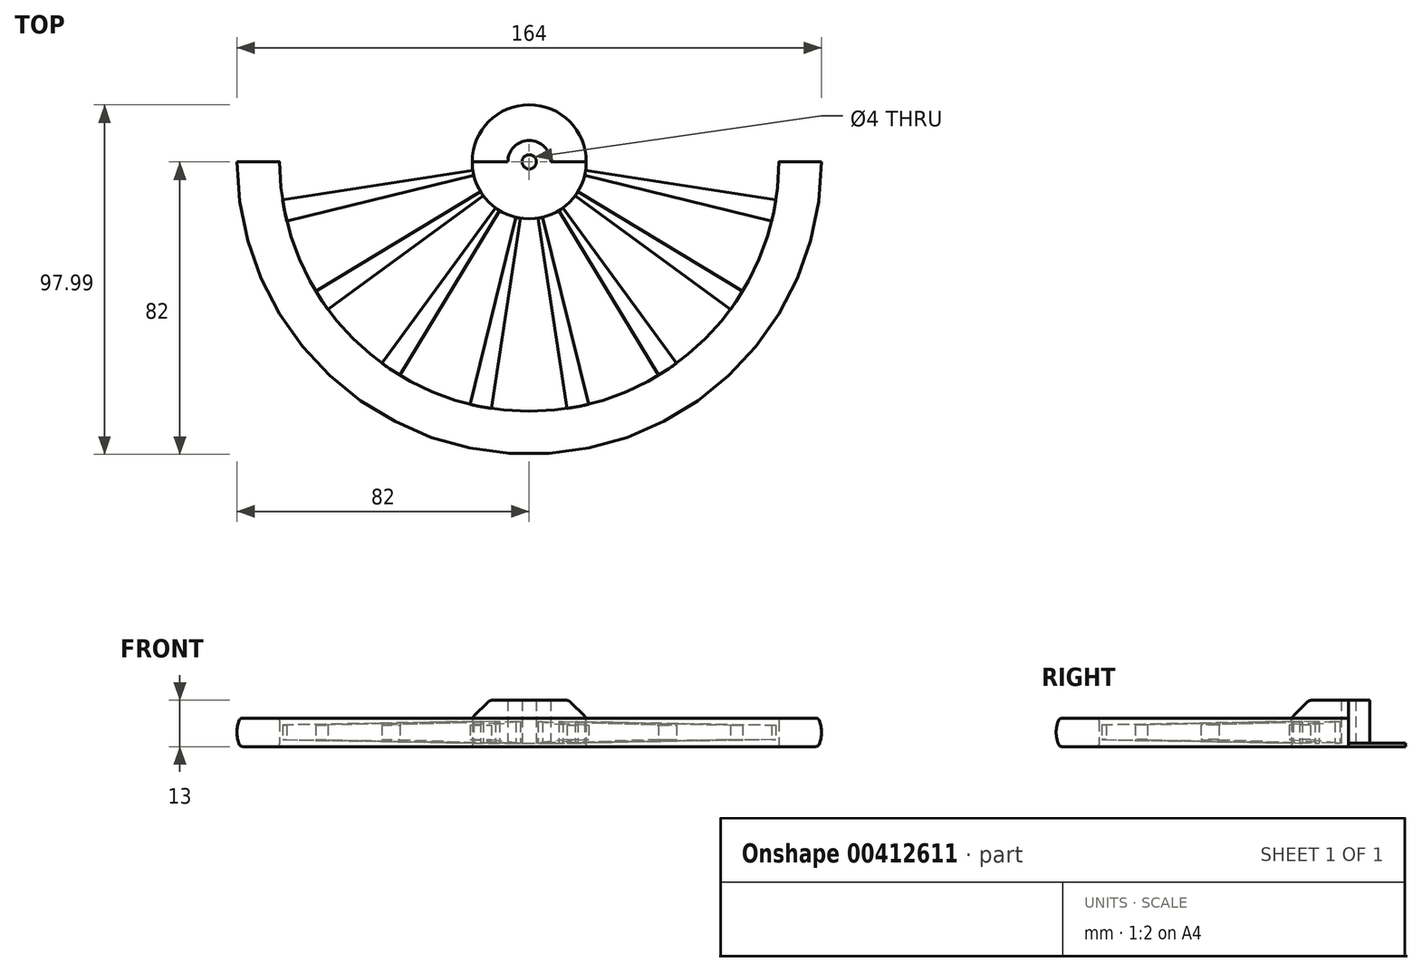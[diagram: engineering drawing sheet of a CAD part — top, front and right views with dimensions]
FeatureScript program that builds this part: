
annotation { "Feature Type Name" : "Feature", "Feature Type Description" : "" }
export const myFeature = defineFeature(function(context is Context, id is Id, definition is map)
    precondition{}
    {
        {
            var Q0;
            Q0=qCreatedBy(makeId("Front.planeOp"),FACE);
            var sketch = newSketch(context, id + "F0", { "sketchPlane" : qUnion([Q0])});
            skLineSegment(sketch, "E0", {"start": v(-2, 0) * mm, "end": v(-2, 13) * mm});
            skLineSegment(sketch, "E1", {"start": v(-2, 13) * mm, "end": v(-10.24, 13) * mm});
            skLineSegment(sketch, "E2", {"start": v(-16, 7.24) * mm, "end": v(-16, 0) * mm});
            skLineSegment(sketch, "E3", {"start": v(-16, 0) * mm, "end": v(-2, 0) * mm});
            skLineSegment(sketch, "E4", {"start": v(-15.4, 8.66) * mm, "end": v(-11.65, 12.41) * mm});
            skPoint(sketch, "E5.visualSharp", {"position": v(-11.07, 13) * mm});
            skArc(sketch, "E5.filletArc", {"start": v(-10.24, 13) * mm, "mid": v(-11, 12.85) * mm, "end": v(-11.65, 12.41) * mm});
            skPoint(sketch, "E6.visualSharp", {"position": v(-16, 8.07) * mm});
            skArc(sketch, "E6.filletArc", {"start": v(-15.4, 8.66) * mm, "mid": v(-15.84, 8) * mm, "end": v(-16, 7.24) * mm});
            skSolve(sketch);
        }
        {
            var Q0;
            Q0=qCreatedBy(makeId("Front.planeOp"),FACE);
            var sketch = newSketch(context, id + "F1", { "sketchPlane" : qUnion([Q0])});
            skLineSegment(sketch, "E7", {"start": v(0, 0) * mm, "end": v(0, 15.4) * mm, "construction": true});
            skSolve(sketch);
        }
        {
            var Q0;
            Q0 = qSketchRegion(id + "F0", true);
            var Q1;
            Q1=sQuery(id+"F1.wireOp",EDGE,"E7");
            revolve(context, id + "F2", {"entities" : qUnion([Q0]), "axis" : qUnion([Q1]), "revolveType" : RevolveType.ONE_DIRECTION, "angle" : 180 * degree});
        }
        {
            var Q0;
            Q0=qCreatedBy(makeId("Front.planeOp"),FACE);
            var sketch = newSketch(context, id + "F3", { "sketchPlane" : qUnion([Q0])});
            skLineSegment(sketch, "E8", {"start": v(-70.8, 0) * mm, "end": v(-80.37, 0) * mm});
            skLineSegment(sketch, "E9", {"start": v(-82, 0) * mm, "end": v(-82, 8) * mm, "construction": true});
            skLineSegment(sketch, "E10", {"start": v(-80.37, 8) * mm, "end": v(-70.75, 8) * mm});
            skLineSegment(sketch, "E11", {"start": v(-70, 7.25) * mm, "end": v(-70, 0.8) * mm});
            skLineSegment(sketch, "E12", {"start": v(-81, 8) * mm, "end": v(-81, 0) * mm, "construction": true});
            skArc(sketch, "E13", {"start": v(-81.3, 7.4) * mm, "mid": v(-82, 4) * mm, "end": v(-81.3, 0.6) * mm});
            skPoint(sketch, "E14.visualSharp", {"position": v(-81, 8) * mm});
            skArc(sketch, "E14.filletArc", {"start": v(-80.37, 8) * mm, "mid": v(-80.92, 7.84) * mm, "end": v(-81.3, 7.4) * mm});
            skPoint(sketch, "E15.visualSharp", {"position": v(-81, 0) * mm});
            skArc(sketch, "E15.filletArc", {"start": v(-81.3, 0.6) * mm, "mid": v(-80.92, 0.16) * mm, "end": v(-80.37, 0) * mm});
            skPoint(sketch, "E16.visualSharp", {"position": v(-70, 8) * mm});
            skArc(sketch, "E16.filletArc", {"start": v(-70, 7.25) * mm, "mid": v(-70.22, 7.78) * mm, "end": v(-70.75, 8) * mm});
            skPoint(sketch, "E17.visualSharp", {"position": v(-70, 0) * mm});
            skArc(sketch, "E17.filletArc", {"start": v(-70.8, 0) * mm, "mid": v(-70.23, 0.23) * mm, "end": v(-70, 0.8) * mm});
            skSolve(sketch);
        }
        {
            var Q0;
            Q0 = qSketchRegion(id + "F3", true);
            var Q1;
            Q1=sQuery(id+"F1.wireOp",EDGE,"E7");
            revolve(context, id + "F4", {"entities" : qUnion([Q0]), "axis" : qUnion([Q1]), "revolveType" : RevolveType.ONE_DIRECTION, "angle" : 180 * degree});
        }
        {
            var Q0;
            Q0=sQuery(id+"F1.wireOp",EDGE,"E7");
            var Q1;
            Q1=qCreatedBy(makeId("Front.planeOp"),FACE);
            cPlane(context, id + "F5", {"entities" : qUnion([Q0, Q1]), "cplaneType" : CPlaneType.LINE_ANGLE, "offset" : 25 * mm, "angle" : 11.25 * degree, "width" : 150 * mm, "height" : 150 * mm});
        }
        {
            var Q0;
            Q0=qCreatedBy(makeId("Top.planeOp"),FACE);
            cPlane(context, id + "F6", {"entities" : qUnion([Q0]), "cplaneType" : CPlaneType.OFFSET, "offset" : 1 * mm, "width" : 150 * mm, "height" : 150 * mm});
        }
        {
            var Q0;
            Q0=qCreatedBy(id+"F6.planeOp",FACE);
            var sketch = newSketch(context, id + "F7", { "sketchPlane" : qUnion([Q0])});
            skLineSegment(sketch, "E18", {"start": v(0, 0) * mm, "end": v(-68.65, -13.66) * mm, "construction": true});
            skLineSegment(sketch, "E19", {"start": v(0, 0) * mm, "end": v(-15.8, -2.43) * mm, "construction": true});
            skLineSegment(sketch, "E20", {"start": v(0, 0) * mm, "end": v(-15.54, -3.8) * mm, "construction": true});
            skLineSegment(sketch, "E21", {"start": v(-15.54, -3.8) * mm, "end": v(-15.54, -3.8) * mm});
            skPoint(sketch, "E22.orphan", {"position": v(-16, 0) * mm});
            skPoint(sketch, "E23.0.start.orphan", {"position": v(16, 0) * mm});
            skLineSegment(sketch, "E24", {"start": v(-15.8, -2.43) * mm, "end": v(-69.19, -10.65) * mm});
            skArc(sketch, "E25", {"start": v(-15.54, -3.8) * mm, "mid": v(-15.69, -3.12) * mm, "end": v(-15.8, -2.43) * mm});
            skLineSegment(sketch, "E26", {"start": v(-15.54, -3.8) * mm, "end": v(-68, -16.64) * mm});
            skArc(sketch, "E27.0", {"start": v(-68, -16.64) * mm, "mid": v(-68.65, -13.66) * mm, "end": v(-69.19, -10.65) * mm});
            skPoint(sketch, "E28.orphan", {"position": v(-70, 0) * mm});
            skPoint(sketch, "E29.orphan", {"position": v(70, 0) * mm});
            skSolve(sketch);
        }
        {
            var Q0;
            Q0 = qSketchRegion(id + "F7", true);
            extrude(context, id + "F8", {"entities" : qUnion([Q0]), "depth" : 6 * mm});
        }
        {
            var Q0;
            Q0=makeQuery(id+"F8.opExtrude","SWEPT_BODY",BODY,{"disambiguationData":[OSD([sQuery(id+"F7.wireOp",EDGE,"E24"),sQuery(id+"F7.wireOp",EDGE,"E25"),sQuery(id+"F7.wireOp",EDGE,"E26"),sQuery(id+"F7.wireOp",EDGE,"E27.0")])]});
            var Q1;
            Q1=sQuery(id+"F1.wireOp",EDGE,"E7");
            circularPattern(context, id + "F9", {"entities" : qUnion([Q0]), "axis" : qUnion([Q1]), "angle" : 157.5 * degree, "instanceCount" : 8, "equalSpace" : true});
        }
        {
            var Q0;
            Q0=qCreatedBy(makeId("Front.planeOp"),FACE);
            var sketch = newSketch(context, id + "F10", { "sketchPlane" : qUnion([Q0])});
            skLineSegment(sketch, "E30.0", {"start": v(-16, 7) * mm, "end": v(-70, 7) * mm});
            skPoint(sketch, "E31.orphan", {"position": v(-16, 7.24) * mm});
            skPoint(sketch, "E32.orphan", {"position": v(-15.8, 7) * mm});
            skLineSegment(sketch, "E33.0", {"start": v(-70, 7) * mm, "end": v(-70, 6.06) * mm});
            skPoint(sketch, "E34.orphan", {"position": v(-69.19, 7) * mm});
            skPoint(sketch, "E35.orphan", {"position": v(-70, 7.25) * mm});
            skLineSegment(sketch, "E36", {"start": v(-16, 7) * mm, "end": v(-70, 6.06) * mm});
            skPoint(sketch, "E37.orphan", {"position": v(-70, 0.8) * mm});
            skPoint(sketch, "E38.0.end.orphan", {"position": v(-16, 0) * mm});
            skSolve(sketch);
        }
        {
            var Q0;
            Q0 = qSketchRegion(id + "F10", true);
            var Q1;
            Q1=sQuery(id+"F1.wireOp",EDGE,"E7");
            revolve(context, id + "F11", {"operationType" : NewBodyOperationType.REMOVE, "entities" : qUnion([Q0]), "axis" : qUnion([Q1]), "revolveType" : RevolveType.FULL, "oppositeDirection" : true});
        }
        {
            var Q0;
            Q0=qCreatedBy(makeId("Front.planeOp"),FACE);
            var sketch = newSketch(context, id + "F12", { "sketchPlane" : qUnion([Q0])});
            skLineSegment(sketch, "E39.0", {"start": v(-70, 1.94) * mm, "end": v(-70, 1) * mm});
            skLineSegment(sketch, "E40.0", {"start": v(-16, 1) * mm, "end": v(-70, 1) * mm});
            skPoint(sketch, "E41.orphan", {"position": v(-69.19, 1) * mm});
            skPoint(sketch, "E42.orphan", {"position": v(-70, 0.8) * mm});
            skPoint(sketch, "E43.orphan", {"position": v(-15.8, 1) * mm});
            skPoint(sketch, "E44.orphan", {"position": v(-16, 0) * mm});
            skLineSegment(sketch, "E45", {"start": v(-16, 1) * mm, "end": v(-70, 1.94) * mm});
            skPoint(sketch, "E46.orphan", {"position": v(-70, 7.25) * mm});
            skPoint(sketch, "E47.0.start.orphan", {"position": v(-16, 7.24) * mm});
            skSolve(sketch);
        }
        {
            var Q0;
            Q0 = qSketchRegion(id + "F12", true);
            var Q1;
            Q1=sQuery(id+"F1.wireOp",EDGE,"E7");
            revolve(context, id + "F13", {"operationType" : NewBodyOperationType.REMOVE, "entities" : qUnion([Q0]), "axis" : qUnion([Q1]), "revolveType" : RevolveType.FULL, "oppositeDirection" : true});
        }
        {
            var Q0;
            Q0=qCreatedBy(makeId("Front.planeOp"),FACE);
            var sketch = newSketch(context, id + "F14", { "sketchPlane" : qUnion([Q0])});
            skLineSegment(sketch, "E48.0", {"start": v(2, 0) * mm, "end": v(2, 13) * mm});
            skLineSegment(sketch, "E49.0", {"start": v(2, 13) * mm, "end": v(6, 13) * mm});
            skLineSegment(sketch, "E50.0", {"start": v(16, 0) * mm, "end": v(2, 0) * mm});
            skLineSegment(sketch, "E51", {"start": v(6, 13) * mm, "end": v(6, 1) * mm});
            skPoint(sketch, "E52.orphan", {"position": v(10.24, 13) * mm});
            skPoint(sketch, "E53.orphan", {"position": v(16, 0) * mm});
            skLineSegment(sketch, "E54.0", {"start": v(16, 1) * mm, "end": v(16, 0) * mm});
            skLineSegment(sketch, "E55", {"start": v(16, 1) * mm, "end": v(6, 1) * mm});
            skPoint(sketch, "E56.orphan", {"position": v(16, 7.24) * mm});
            skSolve(sketch);
        }
        {
            var Q0;
            Q0 = qSketchRegion(id + "F14", true);
            var Q1;
            Q1=sQuery(id+"F1.wireOp",EDGE,"E7");
            revolve(context, id + "F15", {"operationType" : NewBodyOperationType.ADD, "entities" : qUnion([Q0]), "axis" : qUnion([Q1]), "revolveType" : RevolveType.FULL});
        }
    });
